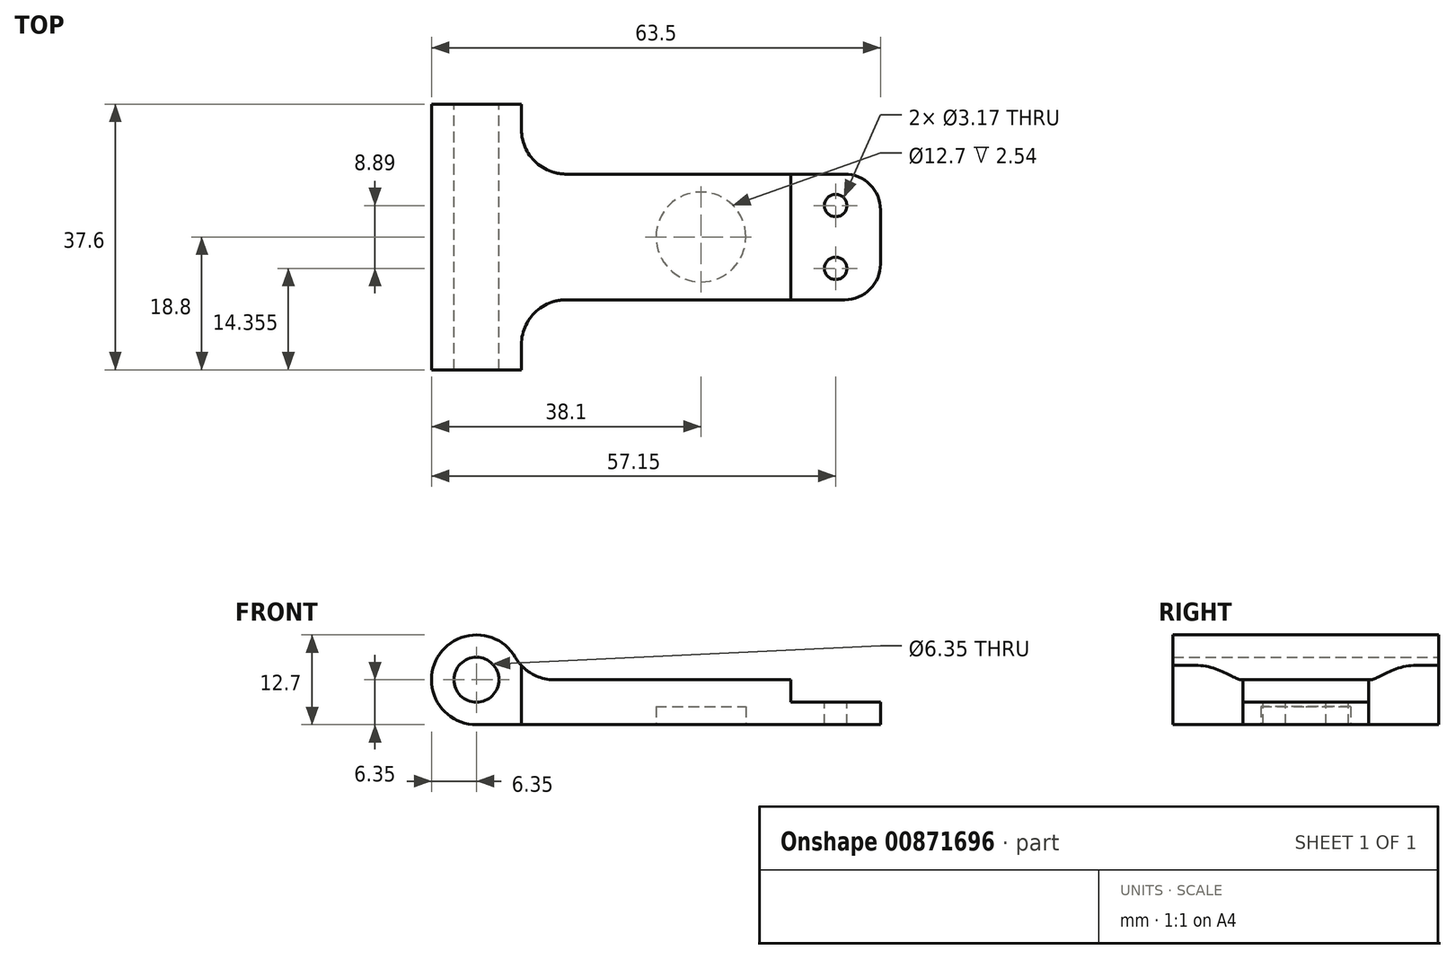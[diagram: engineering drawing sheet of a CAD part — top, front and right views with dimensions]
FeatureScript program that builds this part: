
annotation { "Feature Type Name" : "Feature", "Feature Type Description" : "" }
export const myFeature = defineFeature(function(context is Context, id is Id, definition is map)
    precondition{}
    {
        {
            var Q0;
            Q0=qCreatedBy(makeId("Top.planeOp"),FACE);
            var sketch = newSketch(context, id + "F0", { "sketchPlane" : qUnion([Q0])});
            skLineSegment(sketch, "E0", {"start": v(0, 0) * mm, "end": v(0, 18.8) * mm});
            skLineSegment(sketch, "E1", {"start": v(0, 18.8) * mm, "end": v(12.7, 18.8) * mm});
            skLineSegment(sketch, "E2", {"start": v(12.7, 18.8) * mm, "end": v(12.7, 8.9) * mm});
            skLineSegment(sketch, "E3", {"start": v(12.7, 8.89) * mm, "end": v(63.5, 8.9) * mm});
            skLineSegment(sketch, "E4", {"start": v(63.5, 8.9) * mm, "end": v(63.5, 0) * mm});
            skLineSegment(sketch, "E5.MirrorCS", {"start": v(0, 0) * mm, "end": v(0, -18.8) * mm});
            skLineSegment(sketch, "E6.MirrorCS", {"start": v(0, -18.8) * mm, "end": v(12.7, -18.8) * mm});
            skLineSegment(sketch, "E7.MirrorCS", {"start": v(12.7, -18.8) * mm, "end": v(12.7, -8.9) * mm});
            skLineSegment(sketch, "E8.MirrorCS", {"start": v(12.7, -8.9) * mm, "end": v(63.5, -8.89) * mm});
            skLineSegment(sketch, "E9.MirrorCS", {"start": v(63.5, -8.9) * mm, "end": v(63.5, 0) * mm});
            skSolve(sketch);
        }
        {
            var Q0;
            Q0 = qSketchRegion(id + "F0", true);
            extrude(context, id + "F1", {"entities" : qUnion([Q0]), "depth" : 12.7 * mm, "offsetDistance" : 25.4 * mm});
        }
        {
            var Q0;
            Q0=makeQuery(id+"F1.opExtrude","SWEPT_FACE",FACE,{"disambiguationData":[OSD([sQuery(id+"F0.wireOp",EDGE,"E1")])]});
            var sketch = newSketch(context, id + "F2", { "sketchPlane" : qUnion([Q0])});
            skCircle(sketch, "E10", {"center": v(-6.35, 6.35) * mm, "radius": 3.18 * mm});
            skSolve(sketch);
        }
        {
            var Q0;
            Q0 = qSketchRegion(id + "F2", true);
            extrude(context, id + "F3", {"entities" : qUnion([Q0]), "operationType" : NewBodyOperationType.REMOVE, "endBound" : BoundingType.THROUGH_ALL, "oppositeDirection" : true, "depth" : 25.4 * mm, "offsetDistance" : 25.4 * mm});
        }
        {
            var Q0;
            Q0=makeQuery(id+"F1.opExtrude","SWEPT_EDGE",EDGE,{"disambiguationData":[OSD([sQuery(id+"F0.wireOp",EDGE,"E2"),sQuery(id+"F0.wireOp",EDGE,"E3")])]});
            var Q1;
            Q1=makeQuery(id+"F1.opExtrude","SWEPT_EDGE",EDGE,{"disambiguationData":[OSD([sQuery(id+"F0.wireOp",EDGE,"E7.MirrorCS"),sQuery(id+"F0.wireOp",EDGE,"E8.MirrorCS")])]});
            fillet(context, id + "F4", {"entities" : qUnion([Q0, Q1]), "radius" : 6.35 * mm, "tangentPropagation" : true, "allowEdgeOverflow" : false});
        }
        {
            var Q0;
            Q0=makeQuery(id+"F1.opExtrude","CAP_EDGE",EDGE,{"disambiguationData":[OSD([sQuery(id+"F0.wireOp",EDGE,"E0"),sQuery(id+"F0.wireOp",EDGE,"E5.MirrorCS")])],"isStart":false});
            var Q1;
            Q1=makeQuery(id+"F1.opExtrude","CAP_EDGE",EDGE,{"disambiguationData":[OSD([sQuery(id+"F0.wireOp",EDGE,"E0"),sQuery(id+"F0.wireOp",EDGE,"E5.MirrorCS")])],"isStart":true});
            fillet(context, id + "F5", {"entities" : qUnion([Q0, Q1]), "radius" : 6.35 * mm, "tangentPropagation" : true, "allowEdgeOverflow" : false});
        }
        {
            var Q0;
            Q0=makeQuery(id+"F1.opExtrude","SWEPT_FACE",FACE,{"disambiguationData":[OSD([sQuery(id+"F0.wireOp",EDGE,"E3")])]});
            var sketch = newSketch(context, id + "F6", { "sketchPlane" : qUnion([Q0])});
            skLineSegment(sketch, "E11", {"start": v(-63.5, 12.7) * mm, "end": v(-63.5, 6.35) * mm});
            skArc(sketch, "E12", {"start": v(-12.7, 6.35) * mm, "mid": v(-10.84, 10.84) * mm, "end": v(-6.35, 12.7) * mm});
            skLineSegment(sketch, "E13", {"start": v(-12.7, 6.35) * mm, "end": v(-63.5, 6.35) * mm});
            skLineSegment(sketch, "E14", {"start": v(-63.5, 12.7) * mm, "end": v(-6.35, 12.7) * mm});
            skSolve(sketch);
        }
        {
            var Q0;
            Q0 = qSketchRegion(id + "F6", true);
            extrude(context, id + "F7", {"entities" : qUnion([Q0]), "operationType" : NewBodyOperationType.REMOVE, "endBound" : BoundingType.THROUGH_ALL, "oppositeDirection" : true, "depth" : 25.4 * mm, "offsetDistance" : 25.4 * mm, "hasSecondDirection" : true, "secondDirectionBound" : SecondDirectionBoundingType.THROUGH_ALL, "secondDirectionOppositeDirection" : false, "secondDirectionDepth" : 25.4 * mm});
        }
        {
            var Q0;
            Q0=makeQuery(id+"F7.boolean.opBoolean","COPY",EDGE,{"derivedFrom":makeQuery(id+"F7.opExtrude","SWEPT_EDGE",EDGE,{"disambiguationData":[OSD([sQuery(id+"F6.wireOp",EDGE,"E12"),sQuery(id+"F6.wireOp",EDGE,"E13")])]})});
            fillet(context, id + "F8", {"entities" : qUnion([Q0]), "radius" : 6.35 * mm, "tangentPropagation" : true, "allowEdgeOverflow" : false});
        }
        {
            var Q0;
            Q0=makeQuery(id+"F1.opExtrude","CAP_FACE",FACE,{"disambiguationData":[OSD([sQuery(id+"F0.wireOp",EDGE,"E0"),sQuery(id+"F0.wireOp",EDGE,"E1"),sQuery(id+"F0.wireOp",EDGE,"E2"),sQuery(id+"F0.wireOp",EDGE,"E3"),sQuery(id+"F0.wireOp",EDGE,"E4"),sQuery(id+"F0.wireOp",EDGE,"E5.MirrorCS"),sQuery(id+"F0.wireOp",EDGE,"E6.MirrorCS"),sQuery(id+"F0.wireOp",EDGE,"E7.MirrorCS"),sQuery(id+"F0.wireOp",EDGE,"E8.MirrorCS"),sQuery(id+"F0.wireOp",EDGE,"E9.MirrorCS")])],"isStart":true});
            var sketch = newSketch(context, id + "F9", { "sketchPlane" : qUnion([Q0])});
            skCircle(sketch, "E15", {"center": v(38.1, 0) * mm, "radius": 6.35 * mm});
            skSolve(sketch);
        }
        {
            var Q0;
            Q0 = qSketchRegion(id + "F9", true);
            extrude(context, id + "F10", {"entities" : qUnion([Q0]), "operationType" : NewBodyOperationType.REMOVE, "oppositeDirection" : true, "depth" : 2.54 * mm, "offsetDistance" : 25.4 * mm});
        }
        {
            var Q0;
            Q0=makeQuery(id+"F7.boolean.opBoolean","COPY",FACE,{"derivedFrom":makeQuery(id+"F7.opExtrude","SWEPT_FACE",FACE,{"disambiguationData":[OSD([sQuery(id+"F6.wireOp",EDGE,"E13")])]})});
            var sketch = newSketch(context, id + "F11", { "sketchPlane" : qUnion([Q0])});
            skCircle(sketch, "E16", {"center": v(57.15, 4.45) * mm, "radius": 1.59 * mm});
            skCircle(sketch, "E17", {"center": v(57.15, -4.44) * mm, "radius": 1.59 * mm});
            skSolve(sketch);
        }
        {
            var Q0;
            Q0 = qSketchRegion(id + "F11", true);
            extrude(context, id + "F12", {"entities" : qUnion([Q0]), "operationType" : NewBodyOperationType.REMOVE, "oppositeDirection" : true, "depth" : 25.4 * mm, "offsetDistance" : 25.4 * mm});
        }
        {
            var Q0;
            Q0=makeQuery(id+"F1.opExtrude","SWEPT_EDGE",EDGE,{"disambiguationData":[OSD([sQuery(id+"F0.wireOp",EDGE,"E3"),sQuery(id+"F0.wireOp",EDGE,"E4")])]});
            var Q1;
            Q1=makeQuery(id+"F1.opExtrude","SWEPT_EDGE",EDGE,{"disambiguationData":[OSD([sQuery(id+"F0.wireOp",EDGE,"E8.MirrorCS"),sQuery(id+"F0.wireOp",EDGE,"E9.MirrorCS")])]});
            fillet(context, id + "F13", {"entities" : qUnion([Q0, Q1]), "radius" : 5.08 * mm, "tangentPropagation" : true, "allowEdgeOverflow" : false});
        }
        {
            var Q0;
            Q0=makeQuery(id+"F7.boolean.opBoolean","COPY",FACE,{"derivedFrom":makeQuery(id+"F7.opExtrude","SWEPT_FACE",FACE,{"disambiguationData":[OSD([sQuery(id+"F6.wireOp",EDGE,"E13")])]})});
            var sketch = newSketch(context, id + "F14", { "sketchPlane" : qUnion([Q0])});
            skLineSegment(sketch, "E18.bottom", {"start": v(50.8, -15.5) * mm, "end": v(68.17, -15.5) * mm});
            skLineSegment(sketch, "E18.top", {"start": v(50.8, 12.94) * mm, "end": v(68.17, 12.94) * mm});
            skLineSegment(sketch, "E18.left", {"start": v(50.8, -15.5) * mm, "end": v(50.8, 12.94) * mm});
            skLineSegment(sketch, "E18.right", {"start": v(68.17, -15.5) * mm, "end": v(68.17, 12.94) * mm});
            skSolve(sketch);
        }
        {
            var Q0;
            Q0 = qSketchRegion(id + "F14", true);
            extrude(context, id + "F15", {"entities" : qUnion([Q0]), "operationType" : NewBodyOperationType.REMOVE, "oppositeDirection" : true, "depth" : 3.17 * mm, "offsetDistance" : 25.4 * mm});
        }
    });
